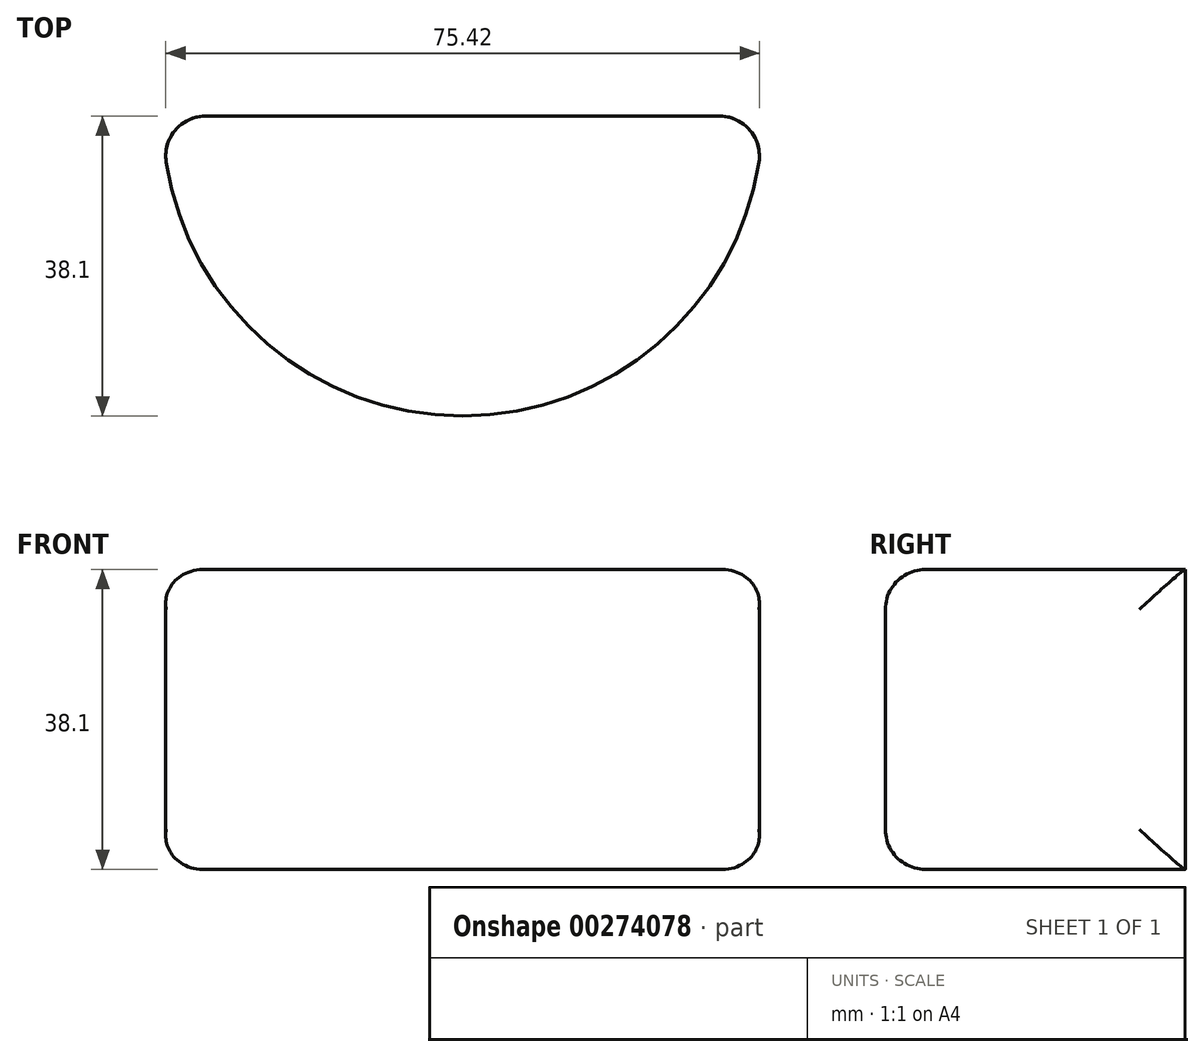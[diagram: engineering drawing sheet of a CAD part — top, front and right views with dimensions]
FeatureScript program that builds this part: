
annotation { "Feature Type Name" : "Feature", "Feature Type Description" : "" }
export const myFeature = defineFeature(function(context is Context, id is Id, definition is map)
    precondition{}
    {
        {
            var Q0;
            Q0=qCreatedBy(makeId("Top.planeOp"),FACE);
            var sketch = newSketch(context, id + "F0", { "sketchPlane" : qUnion([Q0])});
            skArc(sketch, "E0", {"start": v(38.1, 0) * mm, "mid": v(0, -38.1) * mm, "end": v(-38.1, 0) * mm});
            skLineSegment(sketch, "E1", {"start": v(-38.1, 0) * mm, "end": v(38.1, 0) * mm});
            skSolve(sketch);
        }
        {
            var Q0;
            Q0 = qSketchRegion(id + "F0", true);
            extrude(context, id + "F1", {"entities" : qUnion([Q0]), "depth" : 38.1 * mm});
        }
        {
            var Q0;
            Q0=makeQuery(id+"F1.opExtrude","CAP_EDGE",EDGE,{"disambiguationData":[OSD([sQuery(id+"F0.wireOp",EDGE,"E0")])],"isStart":false});
            var Q1;
            Q1=makeQuery(id+"F1.opExtrude","SWEPT_FACE",FACE,{"disambiguationData":[OSD([sQuery(id+"F0.wireOp",EDGE,"E0")])]});
            fillet(context, id + "F2", {"entities" : qUnion([Q0, Q1]), "radius" : 5.08 * mm, "tangentPropagation" : true, "allowEdgeOverflow" : false});
        }
    });
